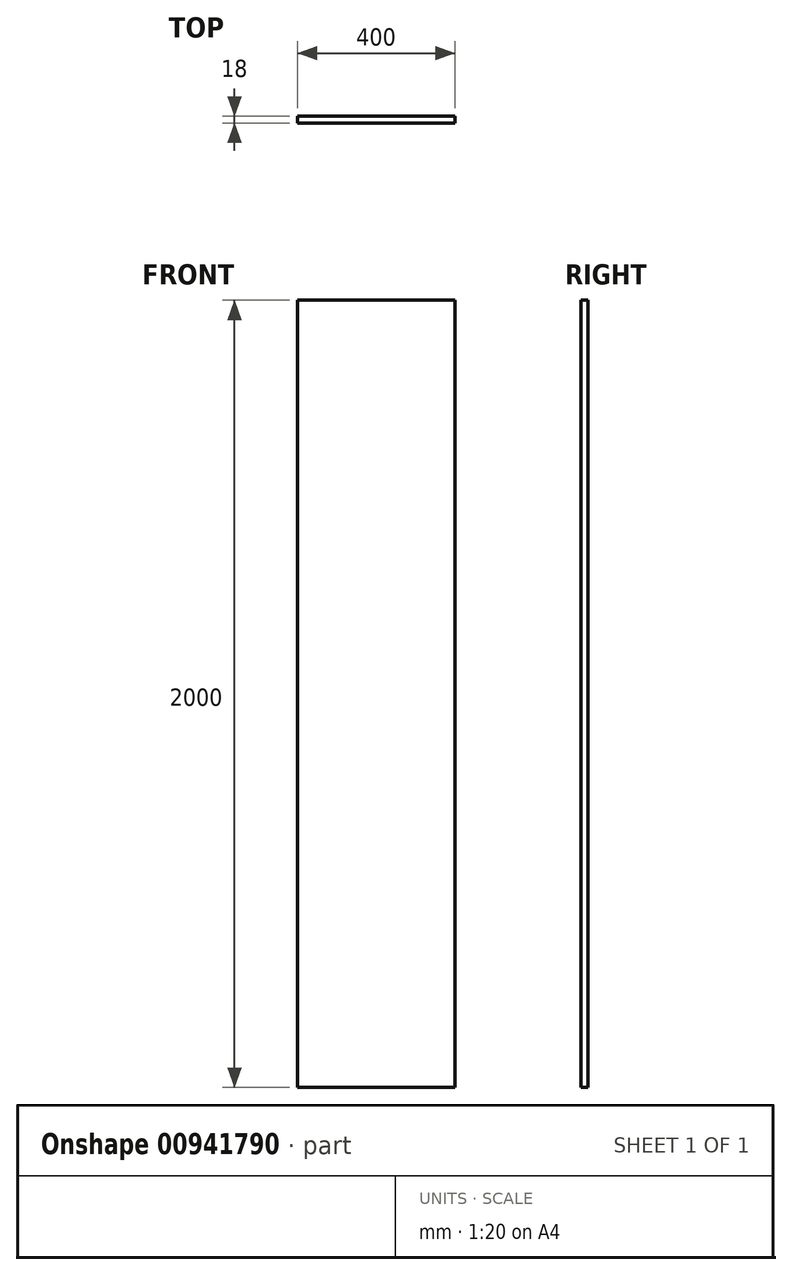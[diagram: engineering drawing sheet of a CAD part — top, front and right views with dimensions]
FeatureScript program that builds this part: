
annotation { "Feature Type Name" : "Feature", "Feature Type Description" : "" }
export const myFeature = defineFeature(function(context is Context, id is Id, definition is map)
    precondition{}
    {
        {
            var Q0;
            Q0=qCreatedBy(makeId("Front.planeOp"),FACE);
            var sketch = newSketch(context, id + "F0", { "sketchPlane" : qUnion([Q0])});
            skLineSegment(sketch, "E0.bottom", {"start": v(216.3, 1000) * mm, "end": v(-183.7, 1000) * mm});
            skLineSegment(sketch, "E0.top", {"start": v(216.3, -1000) * mm, "end": v(-183.7, -1000) * mm});
            skLineSegment(sketch, "E0.left", {"start": v(216.3, 1000) * mm, "end": v(216.3, -1000) * mm});
            skLineSegment(sketch, "E0.right", {"start": v(-183.7, 1000) * mm, "end": v(-183.7, -1000) * mm});
            skPoint(sketch, "E0.middle", {"position": v(16.3, 0) * mm});
            skSolve(sketch);
        }
        {
            var Q0;
            Q0 = qSketchRegion(id + "F0", true);
            extrude(context, id + "F1", {"entities" : qUnion([Q0]), "endBound" : BoundingType.SYMMETRIC, "depth" : 18 * mm, "offsetDistance" : 25 * mm});
        }
    });
